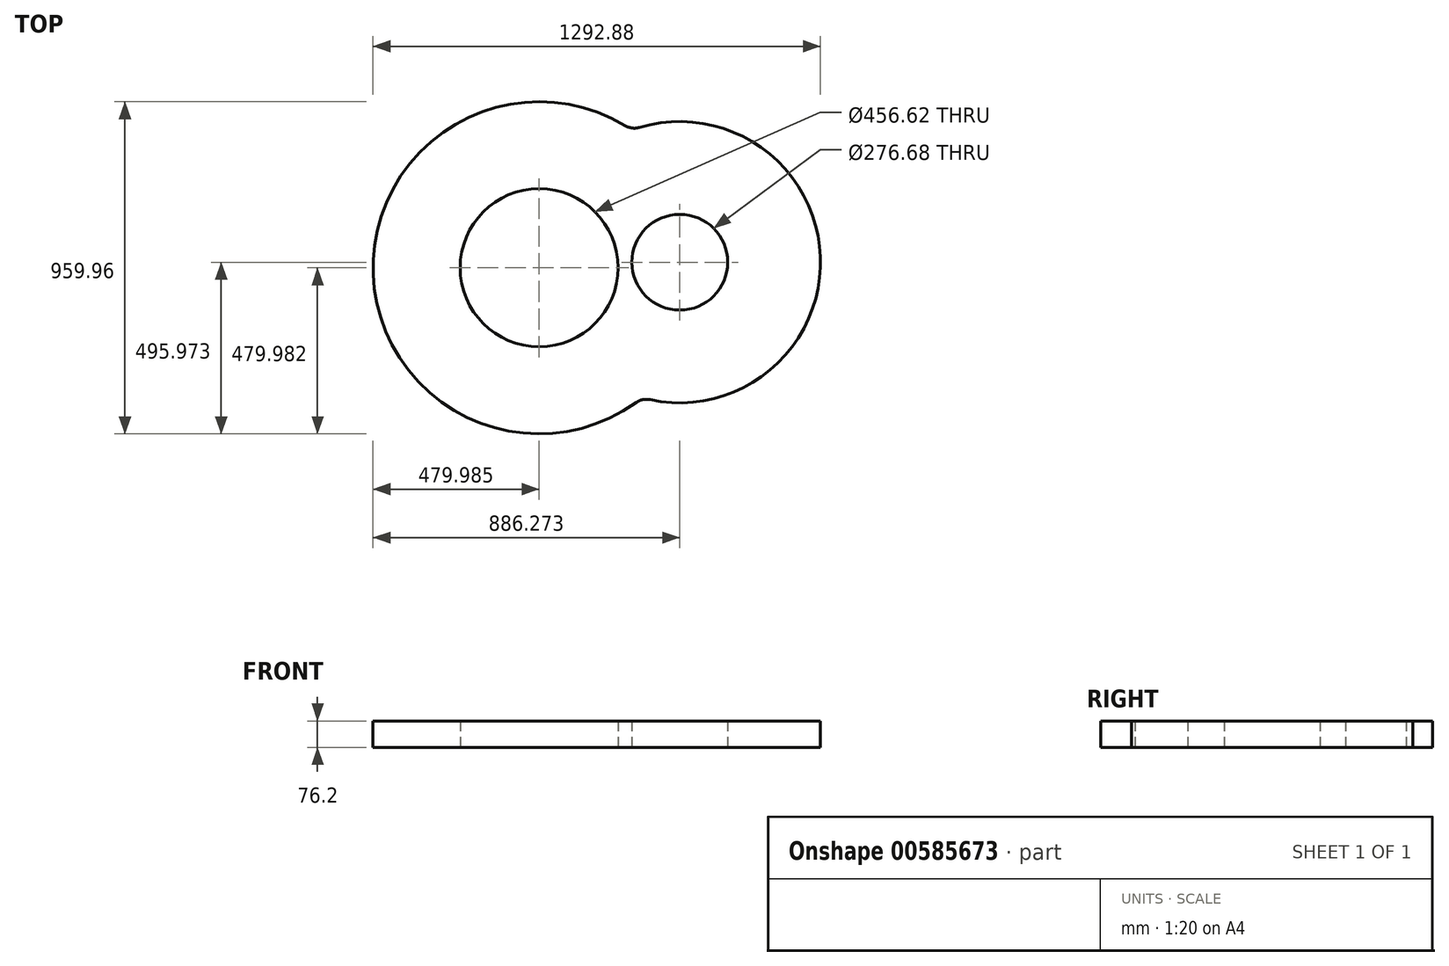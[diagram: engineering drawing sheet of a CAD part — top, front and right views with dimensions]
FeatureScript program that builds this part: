
annotation { "Feature Type Name" : "Feature", "Feature Type Description" : "" }
export const myFeature = defineFeature(function(context is Context, id is Id, definition is map)
    precondition{}
    {
        {
            var Q0;
            Q0=qCreatedBy(makeId("Top.planeOp"),FACE);
            var sketch = newSketch(context, id + "F0", { "sketchPlane" : qUnion([Q0])});
            skArc(sketch, "E0", {"start": v(-20.59, 13.19) * mm, "mid": v(-748.72, -416.33) * mm, "end": v(10.92, -787.28) * mm});
            skPoint(sketch, "E0.first.point", {"position": v(0, 0) * mm});
            skPoint(sketch, "E0.second.point", {"position": v(94.4, -84.01) * mm});
            skPoint(sketch, "E0.third.point", {"position": v(51.53, -40.28) * mm});
            skArc(sketch, "E1", {"start": v(51.29, -778.88) * mm, "mid": v(543.47, -365.47) * mm, "end": v(20.32, 7.99) * mm});
            skPoint(sketch, "E1.first.point", {"position": v(51.53, 16.02) * mm});
            skPoint(sketch, "E1.second.point", {"position": v(277.96, 0) * mm});
            skPoint(sketch, "E2.visualSharp", {"position": v(29.22, -773.46) * mm});
            skArc(sketch, "E2.filletArc", {"start": v(51.29, -778.88) * mm, "mid": v(30.22, -778.8) * mm, "end": v(10.92, -787.28) * mm});
            skArc(sketch, "E3.filletArc", {"start": v(-20.59, 13.19) * mm, "mid": v(-0.68, 6.25) * mm, "end": v(20.32, 7.99) * mm});
            skCircle(sketch, "E4", {"center": v(-269.1, -397.45) * mm, "radius": 228.31 * mm});
            skCircle(sketch, "E5", {"center": v(137.18, -381.46) * mm, "radius": 138.34 * mm});
            skSolve(sketch);
        }
        {
            var Q0;
            Q0 = qSketchRegion(id + "F0", true);
            extrude(context, id + "F1", {"entities" : qUnion([Q0]), "endBound" : BoundingType.SYMMETRIC, "depth" : 76.2 * mm, "offsetDistance" : 25.4 * mm});
        }
    });
